# Revit family: Coat_Hook-Bobrick-Fino_Collection-B-9541
name_source: partatom
category: Specialty Equipment
units: mm (PartAtom-declared; Revit-internal decimal feet)

## family parameters
Cut with Voids When Loaded = No
Host = Face
OmniClass Number = 23.40.20.21.31
OmniClass Title = Robe Hooks
Part Type = Normal
Room Calculation Point = No
Round Connector Dimension = Use Diameter
Shared = Yes

## types (1)
- B-9541
    ADA Compliant = Yes
    Assembly Code = C1030200
    Bumper Depth = 3/16"
    Bumper Diameter = 9/16"
    Default Elevation = 0"
    Description = Fino Collection coat hook with bumper
    Finish = Stainless_Steel-Bobrick-Type_303-Satin_Finish
    Flange Cover Diameter = 1 5/16"
    Flange Cover Thickness = 1/16"
    Hook Pin Diameter = 5/8"
    Installation Type = Wall Mounted
    Length = 3 1/16"
    Load Capacity = 150lbs. (68kg.)
    Manufacturer = Bobrick
    Material = Stainless_Steel-Bobrick-Type_303-Satin_Finish
    Model = B-9541
    Post Diameter = 3/4"
    URL = https://www.bobrick.com
    Warranty Information = 5-Year Limited Warranty

## geometry (parser evidence)
native form markers: Sweep x3
no freeform markers — native parametric forms only
